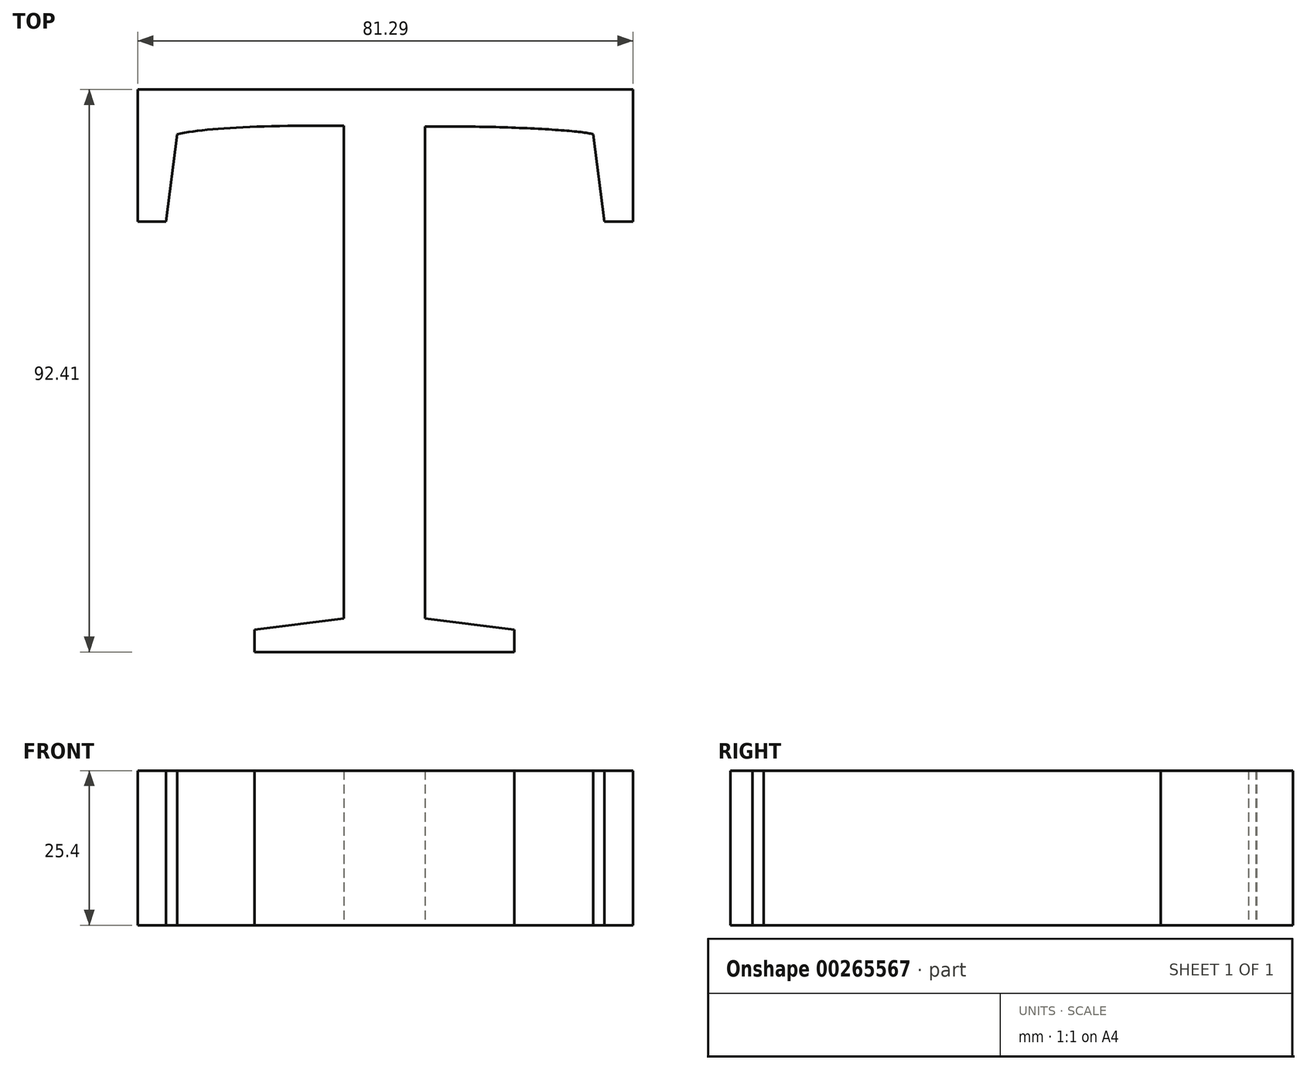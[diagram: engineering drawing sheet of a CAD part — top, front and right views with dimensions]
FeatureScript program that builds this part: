
annotation { "Feature Type Name" : "Feature", "Feature Type Description" : "" }
export const myFeature = defineFeature(function(context is Context, id is Id, definition is map)
    precondition{}
    {
        {
            var Q0;
            Q0=qCreatedBy(makeId("Top.planeOp"),FACE);
            var sketch = newSketch(context, id + "F0", { "sketchPlane" : qUnion([Q0])});
            skText(sketch, "E0", { "text": "T", "fontName": "Tinos-Regular.ttf"});
            const initialGuessF0  = {"E0": [-0.03862, -0.05555, 1, 0, 0.1016]};
            skSetInitialGuess(sketch, initialGuessF0);
            skSolve(sketch);
        }
        {
            var Q0;
            Q0 = qSketchRegion(id + "F0", true);
            extrude(context, id + "F1", {"entities" : qUnion([Q0]), "depth" : 25.4 * mm});
        }
    });
